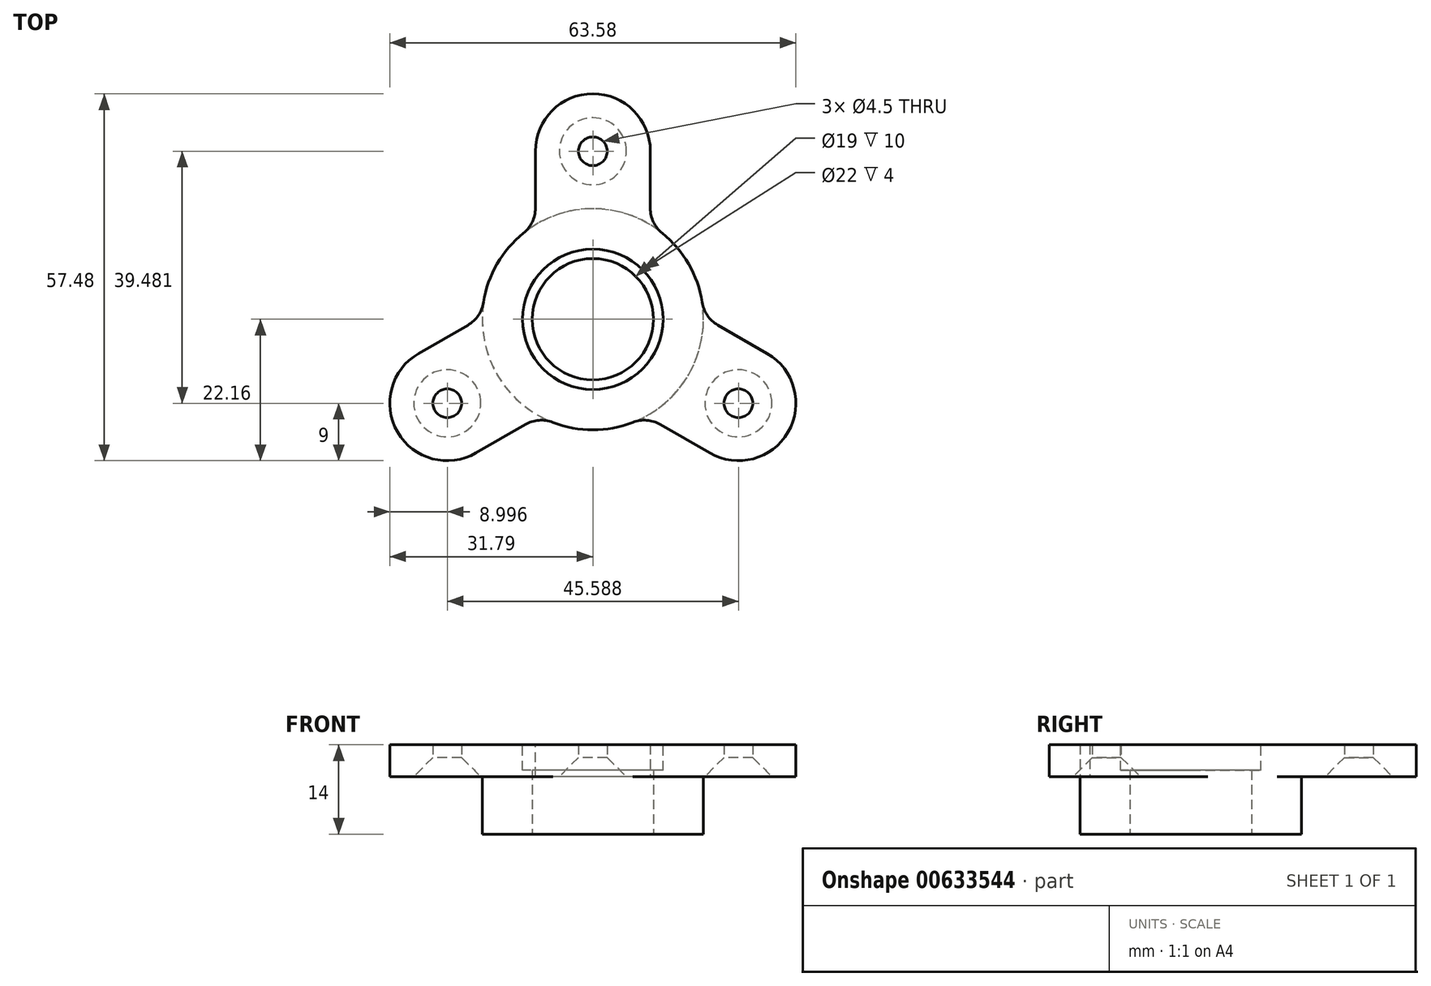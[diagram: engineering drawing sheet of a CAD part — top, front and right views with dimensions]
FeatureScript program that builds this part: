
annotation { "Feature Type Name" : "Feature", "Feature Type Description" : "" }
export const myFeature = defineFeature(function(context is Context, id is Id, definition is map)
    precondition{}
    {
        {
            var Q0;
            Q0=qCreatedBy(makeId("Top.planeOp"),FACE);
            var sketch = newSketch(context, id + "F0", { "sketchPlane" : qUnion([Q0])});
            skLineSegment(sketch, "E0", {"start": v(-30, 17.32) * mm, "end": v(30, 17.32) * mm, "construction": true});
            skLineSegment(sketch, "E1", {"start": v(30, 17.32) * mm, "end": v(0, -34.64) * mm, "construction": true});
            skLineSegment(sketch, "E2", {"start": v(0, -34.64) * mm, "end": v(-30, 17.32) * mm, "construction": true});
            skCircle(sketch, "E3", {"center": v(0, 0) * mm, "radius": 34.64 * mm, "construction": true});
            skLineSegment(sketch, "E4", {"start": v(-9, 26.32) * mm, "end": v(-9, 14.8) * mm});
            skArc(sketch, "E5", {"start": v(-9, 26.32) * mm, "mid": v(-6.36, 32.68) * mm, "end": v(0, 35.32) * mm});
            skArc(sketch, "E6", {"start": v(-9, 14.8) * mm, "mid": v(-12.39, 12.1) * mm, "end": v(-15, 8.66) * mm});
            skLineSegment(sketch, "E7", {"start": v(0, 0) * mm, "end": v(-30, 17.32) * mm, "construction": true});
            skArc(sketch, "E8.MirrorCS", {"start": v(9, 26.32) * mm, "mid": v(6.36, 32.68) * mm, "end": v(0, 35.32) * mm});
            skLineSegment(sketch, "E9.MirrorCS", {"start": v(9, 26.32) * mm, "end": v(9, 14.8) * mm});
            skArc(sketch, "E10.MirrorCS", {"start": v(9, 14.8) * mm, "mid": v(12.39, 12.1) * mm, "end": v(15, 8.66) * mm});
            skCircle(sketch, "E11", {"center": v(0, 26.32) * mm, "radius": 2.25 * mm});
            skCircle(sketch, "E12.1.0", {"center": v(-22.8, -13.16) * mm, "radius": 2.25 * mm});
            skArc(sketch, "E12.1.1", {"start": v(-17.32, 0.4) * mm, "mid": v(-16.68, 4.67) * mm, "end": v(-15, 8.66) * mm});
            skLineSegment(sketch, "E12.1.2", {"start": v(-27.3, -5.37) * mm, "end": v(-17.32, 0.4) * mm});
            skArc(sketch, "E12.1.3", {"start": v(-27.3, -5.37) * mm, "mid": v(-31.49, -10.83) * mm, "end": v(-30.59, -17.66) * mm});
            skArc(sketch, "E12.1.4", {"start": v(-8.32, -15.2) * mm, "mid": v(-4.3, -16.78) * mm, "end": v(0, -17.32) * mm});
            skArc(sketch, "E12.1.5", {"start": v(-18.3, -20.95) * mm, "mid": v(-25.12, -21.85) * mm, "end": v(-30.59, -17.66) * mm});
            skLineSegment(sketch, "E12.1.6", {"start": v(-18.3, -20.95) * mm, "end": v(-8.32, -15.2) * mm});
            skCircle(sketch, "E12.2.0", {"center": v(22.8, -13.16) * mm, "radius": 2.25 * mm});
            skArc(sketch, "E12.2.1", {"start": v(8.32, -15.2) * mm, "mid": v(4.3, -16.78) * mm, "end": v(0, -17.32) * mm});
            skLineSegment(sketch, "E12.2.2", {"start": v(18.3, -20.95) * mm, "end": v(8.32, -15.2) * mm});
            skArc(sketch, "E12.2.3", {"start": v(18.3, -20.95) * mm, "mid": v(25.12, -21.85) * mm, "end": v(30.59, -17.66) * mm});
            skArc(sketch, "E12.2.4", {"start": v(17.32, 0.4) * mm, "mid": v(16.68, 4.67) * mm, "end": v(15, 8.66) * mm});
            skArc(sketch, "E12.2.5", {"start": v(27.3, -5.37) * mm, "mid": v(31.49, -10.83) * mm, "end": v(30.59, -17.66) * mm});
            skLineSegment(sketch, "E12.2.6", {"start": v(27.3, -5.37) * mm, "end": v(17.32, 0.4) * mm});
            skCircle(sketch, "E13", {"center": v(0, 0) * mm, "radius": 9.5 * mm});
            skSolve(sketch);
        }
        {
            var Q0;
            Q0=makeQuery(id+"F0.imprint","IMPRINT",FACE,{"disambiguationData":[TD([[makeQuery(id+"F0.imprint","IMPRINT",EDGE,{"derivedFrom":sQuery(id+"F0.wireOp",EDGE,"E4")}),1.0]])]});
            extrude(context, id + "F1", {"entities" : qUnion([Q0]), "depth" : 5 * mm, "offsetDistance" : 25 * mm});
        }
        {
            var Q0;
            Q0=makeQuery(id+"F1.opExtrude","CAP_FACE",FACE,{"disambiguationData":[OSD([sQuery(id+"F0.wireOp",EDGE,"E4"),sQuery(id+"F0.wireOp",EDGE,"E5"),sQuery(id+"F0.wireOp",EDGE,"E6"),sQuery(id+"F0.wireOp",EDGE,"E8.MirrorCS"),sQuery(id+"F0.wireOp",EDGE,"E9.MirrorCS"),sQuery(id+"F0.wireOp",EDGE,"E10.MirrorCS"),sQuery(id+"F0.wireOp",EDGE,"E11"),sQuery(id+"F0.wireOp",EDGE,"E12.1.0"),sQuery(id+"F0.wireOp",EDGE,"E12.1.1"),sQuery(id+"F0.wireOp",EDGE,"E12.1.2"),sQuery(id+"F0.wireOp",EDGE,"E12.1.3"),sQuery(id+"F0.wireOp",EDGE,"E12.1.4"),sQuery(id+"F0.wireOp",EDGE,"E12.1.5"),sQuery(id+"F0.wireOp",EDGE,"E12.1.6"),sQuery(id+"F0.wireOp",EDGE,"E12.2.0"),sQuery(id+"F0.wireOp",EDGE,"E12.2.1"),sQuery(id+"F0.wireOp",EDGE,"E12.2.2"),sQuery(id+"F0.wireOp",EDGE,"E12.2.3"),sQuery(id+"F0.wireOp",EDGE,"E12.2.4"),sQuery(id+"F0.wireOp",EDGE,"E12.2.5"),sQuery(id+"F0.wireOp",EDGE,"E12.2.6"),sQuery(id+"F0.wireOp",EDGE,"E13")])],"isStart":false});
            var sketch = newSketch(context, id + "F2", { "sketchPlane" : qUnion([Q0])});
            skCircle(sketch, "E14", {"center": v(0, 0) * mm, "radius": 17.32 * mm});
            skSolve(sketch);
        }
        {
            var Q0;
            Q0=makeQuery(id+"F2.imprint","IMPRINT",FACE,{"disambiguationData":[TD([[makeQuery(id+"F2.imprint","IMPRINT",EDGE,{"derivedFrom":makeQuery(id+"F1.opExtrude","CAP_EDGE",EDGE,{"disambiguationData":[OSD([sQuery(id+"F0.wireOp",EDGE,"E13")])],"isStart":false})}),-1.0]])]});
            extrude(context, id + "F3", {"entities" : qUnion([Q0]), "operationType" : NewBodyOperationType.ADD, "oppositeDirection" : true, "depth" : 14 * mm, "offsetDistance" : 25 * mm});
        }
        {
            var Q0;
            Q0=makeQuery(id+"F1.opExtrude","CAP_FACE",FACE,{"disambiguationData":[OSD([sQuery(id+"F0.wireOp",EDGE,"E4"),sQuery(id+"F0.wireOp",EDGE,"E5"),sQuery(id+"F0.wireOp",EDGE,"E6"),sQuery(id+"F0.wireOp",EDGE,"E8.MirrorCS"),sQuery(id+"F0.wireOp",EDGE,"E9.MirrorCS"),sQuery(id+"F0.wireOp",EDGE,"E10.MirrorCS"),sQuery(id+"F0.wireOp",EDGE,"E11"),sQuery(id+"F0.wireOp",EDGE,"E12.1.0"),sQuery(id+"F0.wireOp",EDGE,"E12.1.1"),sQuery(id+"F0.wireOp",EDGE,"E12.1.2"),sQuery(id+"F0.wireOp",EDGE,"E12.1.3"),sQuery(id+"F0.wireOp",EDGE,"E12.1.4"),sQuery(id+"F0.wireOp",EDGE,"E12.1.5"),sQuery(id+"F0.wireOp",EDGE,"E12.1.6"),sQuery(id+"F0.wireOp",EDGE,"E12.2.0"),sQuery(id+"F0.wireOp",EDGE,"E12.2.1"),sQuery(id+"F0.wireOp",EDGE,"E12.2.2"),sQuery(id+"F0.wireOp",EDGE,"E12.2.3"),sQuery(id+"F0.wireOp",EDGE,"E12.2.4"),sQuery(id+"F0.wireOp",EDGE,"E12.2.5"),sQuery(id+"F0.wireOp",EDGE,"E12.2.6"),sQuery(id+"F0.wireOp",EDGE,"E13")])],"isStart":false});
            var sketch = newSketch(context, id + "F4", { "sketchPlane" : qUnion([Q0])});
            skCircle(sketch, "E15", {"center": v(0, 0) * mm, "radius": 11 * mm});
            skSolve(sketch);
        }
        {
            var Q0;
            Q0=makeQuery(id+"F4.imprint","IMPRINT",FACE,{"disambiguationData":[TD([[makeQuery(id+"F4.imprint","IMPRINT",EDGE,{"derivedFrom":sQuery(id+"F4.wireOp",EDGE,"E15")}),1.0]])]});
            extrude(context, id + "F5", {"entities" : qUnion([Q0]), "operationType" : NewBodyOperationType.REMOVE, "oppositeDirection" : true, "depth" : 4 * mm, "offsetDistance" : 25 * mm});
        }
        {
            var Q0;
            Q0=makeQuery(id+"F1.opExtrude","CAP_EDGE",EDGE,{"disambiguationData":[OSD([sQuery(id+"F0.wireOp",EDGE,"E12.1.0")])],"isStart":true});
            var Q1;
            Q1=makeQuery(id+"F1.opExtrude","CAP_EDGE",EDGE,{"disambiguationData":[OSD([sQuery(id+"F0.wireOp",EDGE,"E11")])],"isStart":true});
            var Q2;
            Q2=makeQuery(id+"F1.opExtrude","CAP_EDGE",EDGE,{"disambiguationData":[OSD([sQuery(id+"F0.wireOp",EDGE,"E12.2.0")])],"isStart":true});
            chamfer(context, id + "F6", {"entities" : qUnion([Q0, Q1, Q2]), "width" : 3 * mm, "tangentPropagation" : true});
        }
        {
            var Q0;
            Q0=makeQuery(id+"F1.opExtrude","SWEPT_EDGE",EDGE,{"disambiguationData":[OSD([sQuery(id+"F0.wireOp",EDGE,"E9.MirrorCS"),sQuery(id+"F0.wireOp",EDGE,"E10.MirrorCS")])]});
            var Q1;
            Q1=makeQuery(id+"F1.opExtrude","SWEPT_EDGE",EDGE,{"disambiguationData":[OSD([sQuery(id+"F0.wireOp",EDGE,"E12.2.4"),sQuery(id+"F0.wireOp",EDGE,"E12.2.6")])]});
            var Q2;
            Q2=makeQuery(id+"F1.opExtrude","SWEPT_EDGE",EDGE,{"disambiguationData":[OSD([sQuery(id+"F0.wireOp",EDGE,"E12.1.4"),sQuery(id+"F0.wireOp",EDGE,"E12.1.6")])]});
            var Q3;
            Q3=makeQuery(id+"F1.opExtrude","SWEPT_EDGE",EDGE,{"disambiguationData":[OSD([sQuery(id+"F0.wireOp",EDGE,"E12.2.1"),sQuery(id+"F0.wireOp",EDGE,"E12.2.2")])]});
            var Q4;
            Q4=makeQuery(id+"F1.opExtrude","SWEPT_EDGE",EDGE,{"disambiguationData":[OSD([sQuery(id+"F0.wireOp",EDGE,"E12.1.1"),sQuery(id+"F0.wireOp",EDGE,"E12.1.2")])]});
            var Q5;
            Q5=makeQuery(id+"F1.opExtrude","SWEPT_EDGE",EDGE,{"disambiguationData":[OSD([sQuery(id+"F0.wireOp",EDGE,"E4"),sQuery(id+"F0.wireOp",EDGE,"E6")])]});
            fillet(context, id + "F7", {"entities" : qUnion([Q0, Q1, Q2, Q3, Q4, Q5]), "radius" : 5 * mm, "tangentPropagation" : true, "allowEdgeOverflow" : false});
        }
    });
